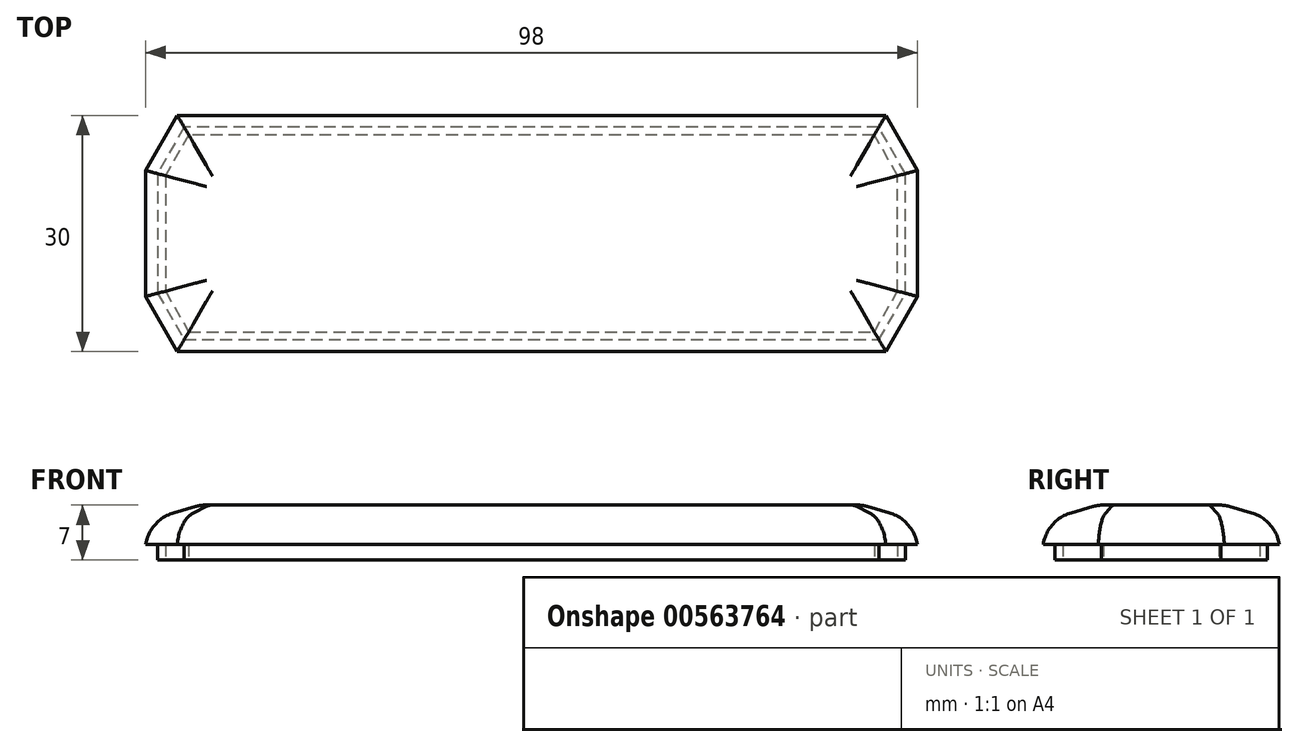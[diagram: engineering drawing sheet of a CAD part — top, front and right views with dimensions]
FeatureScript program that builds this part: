
annotation { "Feature Type Name" : "Feature", "Feature Type Description" : "" }
export const myFeature = defineFeature(function(context is Context, id is Id, definition is map)
    precondition{}
    {
        {
            var Q0;
            Q0=qCreatedBy(makeId("Top.planeOp"),FACE);
            var sketch = newSketch(context, id + "F0", { "sketchPlane" : qUnion([Q0])});
            skLineSegment(sketch, "E0.bottom", {"start": v(-45, 15) * mm, "end": v(45, 15) * mm});
            skLineSegment(sketch, "E0.top", {"start": v(-45, -15) * mm, "end": v(45, -15) * mm});
            skLineSegment(sketch, "E0.left", {"start": v(-45, 15) * mm, "end": v(-45, -15) * mm});
            skLineSegment(sketch, "E0.right", {"start": v(45, 15) * mm, "end": v(45, -15) * mm});
            skLineSegment(sketch, "E1", {"start": v(-75.36, -8) * mm, "end": v(74.95, -8) * mm, "construction": true});
            skLineSegment(sketch, "E2", {"start": v(-74.95, 8) * mm, "end": v(74.95, 8) * mm, "construction": true});
            skLineSegment(sketch, "E3", {"start": v(-49, 8) * mm, "end": v(-49, -8) * mm});
            skLineSegment(sketch, "E4", {"start": v(49, 8) * mm, "end": v(49, -8) * mm});
            skLineSegment(sketch, "E5", {"start": v(-45, 15) * mm, "end": v(-49, 8) * mm});
            skLineSegment(sketch, "E6", {"start": v(-49, -8) * mm, "end": v(-45, -15) * mm});
            skLineSegment(sketch, "E7", {"start": v(45, 15) * mm, "end": v(49, 8) * mm});
            skLineSegment(sketch, "E8", {"start": v(49, -8) * mm, "end": v(45, -15) * mm});
            skSolve(sketch);
        }
        {
            var Q0;
            Q0=makeQuery(id+"F0.imprint","IMPRINT",FACE,{"disambiguationData":[TD([[makeQuery(id+"F0.imprint","IMPRINT",EDGE,{"derivedFrom":sQuery(id+"F0.wireOp",EDGE,"E0.left")}),-1.0]])]});
            var Q1;
            Q1=makeQuery(id+"F0.imprint","IMPRINT",FACE,{"disambiguationData":[TD([[makeQuery(id+"F0.imprint","IMPRINT",EDGE,{"derivedFrom":sQuery(id+"F0.wireOp",EDGE,"E0.right")}),1.0]])]});
            var Q2;
            Q2=makeQuery(id+"F0.imprint","IMPRINT",FACE,{"disambiguationData":[TD([[makeQuery(id+"F0.imprint","IMPRINT",EDGE,{"derivedFrom":sQuery(id+"F0.wireOp",EDGE,"E0.bottom")}),-1.0]])]});
            extrude(context, id + "F1", {"entities" : qUnion([Q0, Q1, Q2]), "depth" : 5 * mm, "offsetDistance" : 25 * mm});
        }
        {
            var Q0;
            Q0=qCreatedBy(makeId("Right.planeOp"),FACE);
            var sketch = newSketch(context, id + "F2", { "sketchPlane" : qUnion([Q0])});
            skLineSegment(sketch, "E9.bottom", {"start": v(-13.5, 0) * mm, "end": v(-12.5, 0) * mm});
            skLineSegment(sketch, "E9.top", {"start": v(-13.5, -2) * mm, "end": v(-12.5, -2) * mm});
            skLineSegment(sketch, "E9.left", {"start": v(-13.5, 0) * mm, "end": v(-13.5, -2) * mm});
            skLineSegment(sketch, "E9.right", {"start": v(-12.5, 0) * mm, "end": v(-12.5, -2) * mm});
            skSolve(sketch);
        }
        {
            var Q0;
            Q0=makeQuery(id+"F2.imprint","IMPRINT",FACE,{"disambiguationData":[TD([[makeQuery(id+"F2.imprint","IMPRINT",EDGE,{"derivedFrom":sQuery(id+"F2.wireOp",EDGE,"E9.bottom")}),-1.0]])]});
            var Q1;
            Q1=makeQuery(id+"F1.opExtrude","CAP_EDGE",EDGE,{"disambiguationData":[OSD([sQuery(id+"F0.wireOp",EDGE,"E0.top")])],"isStart":true});
            var Q2;
            Q2=makeQuery(id+"F1.opExtrude","CAP_EDGE",EDGE,{"disambiguationData":[OSD([sQuery(id+"F0.wireOp",EDGE,"E6")])],"isStart":true});
            var Q3;
            Q3=makeQuery(id+"F1.opExtrude","CAP_EDGE",EDGE,{"disambiguationData":[OSD([sQuery(id+"F0.wireOp",EDGE,"E3")])],"isStart":true});
            var Q4;
            Q4=makeQuery(id+"F1.opExtrude","CAP_EDGE",EDGE,{"disambiguationData":[OSD([sQuery(id+"F0.wireOp",EDGE,"E5")])],"isStart":true});
            var Q5;
            Q5=makeQuery(id+"F1.opExtrude","CAP_EDGE",EDGE,{"disambiguationData":[OSD([sQuery(id+"F0.wireOp",EDGE,"E0.bottom")])],"isStart":true});
            var Q6;
            Q6=makeQuery(id+"F1.opExtrude","CAP_EDGE",EDGE,{"disambiguationData":[OSD([sQuery(id+"F0.wireOp",EDGE,"E7")])],"isStart":true});
            var Q7;
            Q7=makeQuery(id+"F1.opExtrude","CAP_EDGE",EDGE,{"disambiguationData":[OSD([sQuery(id+"F0.wireOp",EDGE,"E4")])],"isStart":true});
            var Q8;
            Q8=makeQuery(id+"F1.opExtrude","CAP_EDGE",EDGE,{"disambiguationData":[OSD([sQuery(id+"F0.wireOp",EDGE,"E8")])],"isStart":true});
            sweep(context, id + "F3", {"operationType" : NewBodyOperationType.ADD, "profiles" : qUnion([Q0]), "path" : qUnion([Q1, Q2, Q3, Q4, Q5, Q6, Q7, Q8])});
        }
        {
            var Q0;
            Q0=makeQuery(id+"F1.opExtrude","CAP_EDGE",EDGE,{"disambiguationData":[OSD([sQuery(id+"F0.wireOp",EDGE,"E3")])],"isStart":false});
            var Q1;
            Q1=makeQuery(id+"F1.opExtrude","CAP_EDGE",EDGE,{"disambiguationData":[OSD([sQuery(id+"F0.wireOp",EDGE,"E6")])],"isStart":false});
            var Q2;
            Q2=makeQuery(id+"F1.opExtrude","CAP_EDGE",EDGE,{"disambiguationData":[OSD([sQuery(id+"F0.wireOp",EDGE,"E5")])],"isStart":false});
            var Q3;
            Q3=makeQuery(id+"F1.opExtrude","CAP_EDGE",EDGE,{"disambiguationData":[OSD([sQuery(id+"F0.wireOp",EDGE,"E8")])],"isStart":false});
            var Q4;
            Q4=makeQuery(id+"F1.opExtrude","CAP_EDGE",EDGE,{"disambiguationData":[OSD([sQuery(id+"F0.wireOp",EDGE,"E4")])],"isStart":false});
            var Q5;
            Q5=makeQuery(id+"F1.opExtrude","CAP_EDGE",EDGE,{"disambiguationData":[OSD([sQuery(id+"F0.wireOp",EDGE,"E7")])],"isStart":false});
            var Q6;
            Q6=makeQuery(id+"F1.opExtrude","CAP_EDGE",EDGE,{"disambiguationData":[OSD([sQuery(id+"F0.wireOp",EDGE,"E0.top")])],"isStart":false});
            var Q7;
            Q7=makeQuery(id+"F1.opExtrude","CAP_EDGE",EDGE,{"disambiguationData":[OSD([sQuery(id+"F0.wireOp",EDGE,"E0.bottom")])],"isStart":false});
            chamfer(context, id + "F4", {"entities" : qUnion([Q0, Q1, Q2, Q3, Q4, Q5, Q6, Q7]), "chamferType" : ChamferType.TWO_OFFSETS, "width1" : 7 * mm, "oppositeDirection" : false, "width2" : 2 * mm, "tangentPropagation" : true});
        }
        {
            var Q0;
            {var subQ0=sQuery(id+"F0.wireOp",EDGE,"E0.bottom");Q0=makeQuery(id+"F4.opChamfer","BLEND_EDGE",EDGE,{"blendedFrom":[makeQuery(id+"F1.opExtrude","CAP_EDGE",EDGE,{"disambiguationData":[OSD([subQ0])],"isStart":false}),makeQuery(id+"F1.opExtrude","SWEPT_FACE",FACE,{"disambiguationData":[OSD([subQ0])]})],"blendedInto":[makeQuery(id+"F1.opExtrude","SWEPT_FACE",FACE,{"disambiguationData":[OSD([subQ0])]})]});}
            var Q1;
            {var subQ0=sQuery(id+"F0.wireOp",EDGE,"E0.bottom");Q1=makeQuery(id+"F4.opChamfer","BLEND_EDGE",EDGE,{"blendedFrom":[makeQuery(id+"F1.opExtrude","CAP_EDGE",EDGE,{"disambiguationData":[OSD([subQ0])],"isStart":false}),makeQuery(id+"F1.opExtrude","CAP_FACE",FACE,{"disambiguationData":[OSD([subQ0,sQuery(id+"F0.wireOp",EDGE,"E0.top"),sQuery(id+"F0.wireOp",EDGE,"E3"),sQuery(id+"F0.wireOp",EDGE,"E4"),sQuery(id+"F0.wireOp",EDGE,"E5"),sQuery(id+"F0.wireOp",EDGE,"E6"),sQuery(id+"F0.wireOp",EDGE,"E7"),sQuery(id+"F0.wireOp",EDGE,"E8")])],"isStart":false})],"blendedInto":[makeQuery(id+"F1.opExtrude","CAP_FACE",FACE,{"disambiguationData":[OSD([subQ0,sQuery(id+"F0.wireOp",EDGE,"E0.top"),sQuery(id+"F0.wireOp",EDGE,"E3"),sQuery(id+"F0.wireOp",EDGE,"E4"),sQuery(id+"F0.wireOp",EDGE,"E5"),sQuery(id+"F0.wireOp",EDGE,"E6"),sQuery(id+"F0.wireOp",EDGE,"E7"),sQuery(id+"F0.wireOp",EDGE,"E8")])],"isStart":false})]});}
            var Q2;
            {var subQ0=sQuery(id+"F0.wireOp",EDGE,"E0.top");Q2=makeQuery(id+"F4.opChamfer","BLEND_EDGE",EDGE,{"blendedFrom":[makeQuery(id+"F1.opExtrude","CAP_EDGE",EDGE,{"disambiguationData":[OSD([subQ0])],"isStart":false}),makeQuery(id+"F1.opExtrude","CAP_FACE",FACE,{"disambiguationData":[OSD([sQuery(id+"F0.wireOp",EDGE,"E0.bottom"),subQ0,sQuery(id+"F0.wireOp",EDGE,"E3"),sQuery(id+"F0.wireOp",EDGE,"E4"),sQuery(id+"F0.wireOp",EDGE,"E5"),sQuery(id+"F0.wireOp",EDGE,"E6"),sQuery(id+"F0.wireOp",EDGE,"E7"),sQuery(id+"F0.wireOp",EDGE,"E8")])],"isStart":false})],"blendedInto":[makeQuery(id+"F1.opExtrude","CAP_FACE",FACE,{"disambiguationData":[OSD([sQuery(id+"F0.wireOp",EDGE,"E0.bottom"),subQ0,sQuery(id+"F0.wireOp",EDGE,"E3"),sQuery(id+"F0.wireOp",EDGE,"E4"),sQuery(id+"F0.wireOp",EDGE,"E5"),sQuery(id+"F0.wireOp",EDGE,"E6"),sQuery(id+"F0.wireOp",EDGE,"E7"),sQuery(id+"F0.wireOp",EDGE,"E8")])],"isStart":false})]});}
            var Q3;
            {var subQ0=sQuery(id+"F0.wireOp",EDGE,"E0.top");Q3=makeQuery(id+"F4.opChamfer","BLEND_EDGE",EDGE,{"blendedFrom":[makeQuery(id+"F1.opExtrude","CAP_EDGE",EDGE,{"disambiguationData":[OSD([subQ0])],"isStart":false}),makeQuery(id+"F1.opExtrude","SWEPT_FACE",FACE,{"disambiguationData":[OSD([subQ0])]})],"blendedInto":[makeQuery(id+"F1.opExtrude","SWEPT_FACE",FACE,{"disambiguationData":[OSD([subQ0])]})]});}
            var Q4;
            {var subQ0=sQuery(id+"F0.wireOp",EDGE,"E6");Q4=makeQuery(id+"F4.opChamfer","BLEND_EDGE",EDGE,{"blendedFrom":[makeQuery(id+"F1.opExtrude","CAP_EDGE",EDGE,{"disambiguationData":[OSD([subQ0])],"isStart":false}),makeQuery(id+"F1.opExtrude","SWEPT_FACE",FACE,{"disambiguationData":[OSD([subQ0])]})],"blendedInto":[makeQuery(id+"F1.opExtrude","SWEPT_FACE",FACE,{"disambiguationData":[OSD([subQ0])]})]});}
            var Q5;
            {var subQ0=sQuery(id+"F0.wireOp",EDGE,"E3");Q5=makeQuery(id+"F4.opChamfer","BLEND_EDGE",EDGE,{"blendedFrom":[makeQuery(id+"F1.opExtrude","CAP_EDGE",EDGE,{"disambiguationData":[OSD([subQ0])],"isStart":false}),makeQuery(id+"F1.opExtrude","CAP_FACE",FACE,{"disambiguationData":[OSD([sQuery(id+"F0.wireOp",EDGE,"E0.bottom"),sQuery(id+"F0.wireOp",EDGE,"E0.top"),subQ0,sQuery(id+"F0.wireOp",EDGE,"E4"),sQuery(id+"F0.wireOp",EDGE,"E5"),sQuery(id+"F0.wireOp",EDGE,"E6"),sQuery(id+"F0.wireOp",EDGE,"E7"),sQuery(id+"F0.wireOp",EDGE,"E8")])],"isStart":false})],"blendedInto":[makeQuery(id+"F1.opExtrude","CAP_FACE",FACE,{"disambiguationData":[OSD([sQuery(id+"F0.wireOp",EDGE,"E0.bottom"),sQuery(id+"F0.wireOp",EDGE,"E0.top"),subQ0,sQuery(id+"F0.wireOp",EDGE,"E4"),sQuery(id+"F0.wireOp",EDGE,"E5"),sQuery(id+"F0.wireOp",EDGE,"E6"),sQuery(id+"F0.wireOp",EDGE,"E7"),sQuery(id+"F0.wireOp",EDGE,"E8")])],"isStart":false})]});}
            var Q6;
            {var subQ0=sQuery(id+"F0.wireOp",EDGE,"E3");Q6=makeQuery(id+"F4.opChamfer","BLEND_EDGE",EDGE,{"blendedFrom":[makeQuery(id+"F1.opExtrude","CAP_EDGE",EDGE,{"disambiguationData":[OSD([subQ0])],"isStart":false}),makeQuery(id+"F1.opExtrude","SWEPT_FACE",FACE,{"disambiguationData":[OSD([subQ0])]})],"blendedInto":[makeQuery(id+"F1.opExtrude","SWEPT_FACE",FACE,{"disambiguationData":[OSD([subQ0])]})]});}
            var Q7;
            {var subQ0=sQuery(id+"F0.wireOp",EDGE,"E6");Q7=makeQuery(id+"F4.opChamfer","BLEND_EDGE",EDGE,{"blendedFrom":[makeQuery(id+"F1.opExtrude","CAP_EDGE",EDGE,{"disambiguationData":[OSD([subQ0])],"isStart":false}),makeQuery(id+"F1.opExtrude","CAP_FACE",FACE,{"disambiguationData":[OSD([sQuery(id+"F0.wireOp",EDGE,"E0.bottom"),sQuery(id+"F0.wireOp",EDGE,"E0.top"),sQuery(id+"F0.wireOp",EDGE,"E3"),sQuery(id+"F0.wireOp",EDGE,"E4"),sQuery(id+"F0.wireOp",EDGE,"E5"),subQ0,sQuery(id+"F0.wireOp",EDGE,"E7"),sQuery(id+"F0.wireOp",EDGE,"E8")])],"isStart":false})],"blendedInto":[makeQuery(id+"F1.opExtrude","CAP_FACE",FACE,{"disambiguationData":[OSD([sQuery(id+"F0.wireOp",EDGE,"E0.bottom"),sQuery(id+"F0.wireOp",EDGE,"E0.top"),sQuery(id+"F0.wireOp",EDGE,"E3"),sQuery(id+"F0.wireOp",EDGE,"E4"),sQuery(id+"F0.wireOp",EDGE,"E5"),subQ0,sQuery(id+"F0.wireOp",EDGE,"E7"),sQuery(id+"F0.wireOp",EDGE,"E8")])],"isStart":false})]});}
            var Q8;
            {var subQ0=sQuery(id+"F0.wireOp",EDGE,"E5");Q8=makeQuery(id+"F4.opChamfer","BLEND_EDGE",EDGE,{"blendedFrom":[makeQuery(id+"F1.opExtrude","CAP_EDGE",EDGE,{"disambiguationData":[OSD([subQ0])],"isStart":false}),makeQuery(id+"F1.opExtrude","SWEPT_FACE",FACE,{"disambiguationData":[OSD([subQ0])]})],"blendedInto":[makeQuery(id+"F1.opExtrude","SWEPT_FACE",FACE,{"disambiguationData":[OSD([subQ0])]})]});}
            var Q9;
            {var subQ0=sQuery(id+"F0.wireOp",EDGE,"E5");Q9=makeQuery(id+"F4.opChamfer","BLEND_EDGE",EDGE,{"blendedFrom":[makeQuery(id+"F1.opExtrude","CAP_EDGE",EDGE,{"disambiguationData":[OSD([subQ0])],"isStart":false}),makeQuery(id+"F1.opExtrude","CAP_FACE",FACE,{"disambiguationData":[OSD([sQuery(id+"F0.wireOp",EDGE,"E0.bottom"),sQuery(id+"F0.wireOp",EDGE,"E0.top"),sQuery(id+"F0.wireOp",EDGE,"E3"),sQuery(id+"F0.wireOp",EDGE,"E4"),subQ0,sQuery(id+"F0.wireOp",EDGE,"E6"),sQuery(id+"F0.wireOp",EDGE,"E7"),sQuery(id+"F0.wireOp",EDGE,"E8")])],"isStart":false})],"blendedInto":[makeQuery(id+"F1.opExtrude","CAP_FACE",FACE,{"disambiguationData":[OSD([sQuery(id+"F0.wireOp",EDGE,"E0.bottom"),sQuery(id+"F0.wireOp",EDGE,"E0.top"),sQuery(id+"F0.wireOp",EDGE,"E3"),sQuery(id+"F0.wireOp",EDGE,"E4"),subQ0,sQuery(id+"F0.wireOp",EDGE,"E6"),sQuery(id+"F0.wireOp",EDGE,"E7"),sQuery(id+"F0.wireOp",EDGE,"E8")])],"isStart":false})]});}
            var Q10;
            {var subQ0=sQuery(id+"F0.wireOp",EDGE,"E4");Q10=makeQuery(id+"F4.opChamfer","BLEND_EDGE",EDGE,{"blendedFrom":[makeQuery(id+"F1.opExtrude","CAP_EDGE",EDGE,{"disambiguationData":[OSD([subQ0])],"isStart":false}),makeQuery(id+"F1.opExtrude","SWEPT_FACE",FACE,{"disambiguationData":[OSD([subQ0])]})],"blendedInto":[makeQuery(id+"F1.opExtrude","SWEPT_FACE",FACE,{"disambiguationData":[OSD([subQ0])]})]});}
            var Q11;
            {var subQ0=sQuery(id+"F0.wireOp",EDGE,"E7");Q11=makeQuery(id+"F4.opChamfer","BLEND_EDGE",EDGE,{"blendedFrom":[makeQuery(id+"F1.opExtrude","CAP_EDGE",EDGE,{"disambiguationData":[OSD([subQ0])],"isStart":false}),makeQuery(id+"F1.opExtrude","SWEPT_FACE",FACE,{"disambiguationData":[OSD([subQ0])]})],"blendedInto":[makeQuery(id+"F1.opExtrude","SWEPT_FACE",FACE,{"disambiguationData":[OSD([subQ0])]})]});}
            var Q12;
            {var subQ0=sQuery(id+"F0.wireOp",EDGE,"E7");Q12=makeQuery(id+"F4.opChamfer","BLEND_EDGE",EDGE,{"blendedFrom":[makeQuery(id+"F1.opExtrude","CAP_EDGE",EDGE,{"disambiguationData":[OSD([subQ0])],"isStart":false}),makeQuery(id+"F1.opExtrude","CAP_FACE",FACE,{"disambiguationData":[OSD([sQuery(id+"F0.wireOp",EDGE,"E0.bottom"),sQuery(id+"F0.wireOp",EDGE,"E0.top"),sQuery(id+"F0.wireOp",EDGE,"E3"),sQuery(id+"F0.wireOp",EDGE,"E4"),sQuery(id+"F0.wireOp",EDGE,"E5"),sQuery(id+"F0.wireOp",EDGE,"E6"),subQ0,sQuery(id+"F0.wireOp",EDGE,"E8")])],"isStart":false})],"blendedInto":[makeQuery(id+"F1.opExtrude","CAP_FACE",FACE,{"disambiguationData":[OSD([sQuery(id+"F0.wireOp",EDGE,"E0.bottom"),sQuery(id+"F0.wireOp",EDGE,"E0.top"),sQuery(id+"F0.wireOp",EDGE,"E3"),sQuery(id+"F0.wireOp",EDGE,"E4"),sQuery(id+"F0.wireOp",EDGE,"E5"),sQuery(id+"F0.wireOp",EDGE,"E6"),subQ0,sQuery(id+"F0.wireOp",EDGE,"E8")])],"isStart":false})]});}
            var Q13;
            {var subQ0=sQuery(id+"F0.wireOp",EDGE,"E8");Q13=makeQuery(id+"F4.opChamfer","BLEND_EDGE",EDGE,{"blendedFrom":[makeQuery(id+"F1.opExtrude","CAP_EDGE",EDGE,{"disambiguationData":[OSD([subQ0])],"isStart":false}),makeQuery(id+"F1.opExtrude","CAP_FACE",FACE,{"disambiguationData":[OSD([sQuery(id+"F0.wireOp",EDGE,"E0.bottom"),sQuery(id+"F0.wireOp",EDGE,"E0.top"),sQuery(id+"F0.wireOp",EDGE,"E3"),sQuery(id+"F0.wireOp",EDGE,"E4"),sQuery(id+"F0.wireOp",EDGE,"E5"),sQuery(id+"F0.wireOp",EDGE,"E6"),sQuery(id+"F0.wireOp",EDGE,"E7"),subQ0])],"isStart":false})],"blendedInto":[makeQuery(id+"F1.opExtrude","CAP_FACE",FACE,{"disambiguationData":[OSD([sQuery(id+"F0.wireOp",EDGE,"E0.bottom"),sQuery(id+"F0.wireOp",EDGE,"E0.top"),sQuery(id+"F0.wireOp",EDGE,"E3"),sQuery(id+"F0.wireOp",EDGE,"E4"),sQuery(id+"F0.wireOp",EDGE,"E5"),sQuery(id+"F0.wireOp",EDGE,"E6"),sQuery(id+"F0.wireOp",EDGE,"E7"),subQ0])],"isStart":false})]});}
            var Q14;
            {var subQ0=sQuery(id+"F0.wireOp",EDGE,"E8");Q14=makeQuery(id+"F4.opChamfer","BLEND_EDGE",EDGE,{"blendedFrom":[makeQuery(id+"F1.opExtrude","CAP_EDGE",EDGE,{"disambiguationData":[OSD([subQ0])],"isStart":false}),makeQuery(id+"F1.opExtrude","SWEPT_FACE",FACE,{"disambiguationData":[OSD([subQ0])]})],"blendedInto":[makeQuery(id+"F1.opExtrude","SWEPT_FACE",FACE,{"disambiguationData":[OSD([subQ0])]})]});}
            var Q15;
            {var subQ0=sQuery(id+"F0.wireOp",EDGE,"E4");Q15=makeQuery(id+"F4.opChamfer","BLEND_EDGE",EDGE,{"blendedFrom":[makeQuery(id+"F1.opExtrude","CAP_EDGE",EDGE,{"disambiguationData":[OSD([subQ0])],"isStart":false}),makeQuery(id+"F1.opExtrude","CAP_FACE",FACE,{"disambiguationData":[OSD([sQuery(id+"F0.wireOp",EDGE,"E0.bottom"),sQuery(id+"F0.wireOp",EDGE,"E0.top"),sQuery(id+"F0.wireOp",EDGE,"E3"),subQ0,sQuery(id+"F0.wireOp",EDGE,"E5"),sQuery(id+"F0.wireOp",EDGE,"E6"),sQuery(id+"F0.wireOp",EDGE,"E7"),sQuery(id+"F0.wireOp",EDGE,"E8")])],"isStart":false})],"blendedInto":[makeQuery(id+"F1.opExtrude","CAP_FACE",FACE,{"disambiguationData":[OSD([sQuery(id+"F0.wireOp",EDGE,"E0.bottom"),sQuery(id+"F0.wireOp",EDGE,"E0.top"),sQuery(id+"F0.wireOp",EDGE,"E3"),subQ0,sQuery(id+"F0.wireOp",EDGE,"E5"),sQuery(id+"F0.wireOp",EDGE,"E6"),sQuery(id+"F0.wireOp",EDGE,"E7"),sQuery(id+"F0.wireOp",EDGE,"E8")])],"isStart":false})]});}
            fillet(context, id + "F5", {"entities" : qUnion([Q0, Q1, Q2, Q3, Q4, Q5, Q6, Q7, Q8, Q9, Q10, Q11, Q12, Q13, Q14, Q15]), "radius" : 5 * mm, "tangentPropagation" : true, "allowEdgeOverflow" : false});
        }
    });
